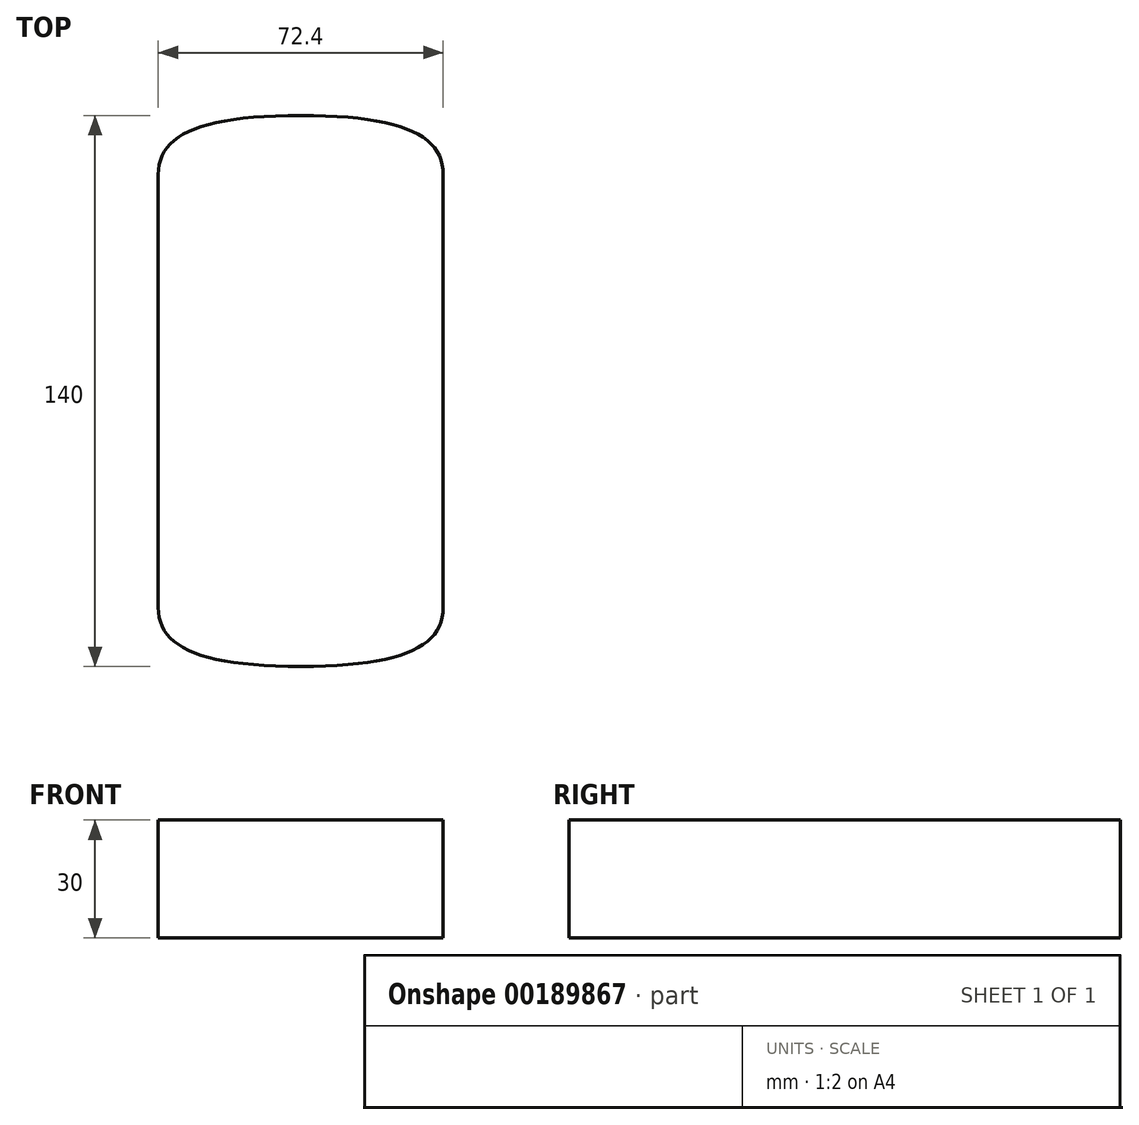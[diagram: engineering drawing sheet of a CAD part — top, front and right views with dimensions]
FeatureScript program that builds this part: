
annotation { "Feature Type Name" : "Feature", "Feature Type Description" : "" }
export const myFeature = defineFeature(function(context is Context, id is Id, definition is map)
    precondition{}
    {
        {
            var Q0;
            Q0=qCreatedBy(makeId("Top.planeOp"),FACE);
            var sketch = newSketch(context, id + "F0", { "sketchPlane" : qUnion([Q0])});
            skLineSegment(sketch, "E0", {"start": v(-36.2, 0) * mm, "end": v(-36.2, 55) * mm});
            skFitSpline(sketch, "E1", {"points": [v(-36.2, 55) * mm, v(0, 70) * mm], "startDerivative": vector(0, 30) * mm, "endDerivative": vector(76.78, 0) * mm});
            skLineSegment(sketch, "E2", {"start": v(0, 70) * mm, "end": v(0, 0) * mm});
            skLineSegment(sketch, "E3", {"start": v(0, 0) * mm, "end": v(-36.2, 0) * mm});
            skSolve(sketch);
        }
        {
            var Q0;
            Q0=makeQuery(id+"F0.imprint","IMPRINT",FACE,{"disambiguationData":[TD([[makeQuery(id+"F0.imprint","IMPRINT",EDGE,{"derivedFrom":sQuery(id+"F0.wireOp",EDGE,"E0")}),-1.0]])]});
            extrude(context, id + "F1", {"entities" : qUnion([Q0]), "depth" : 30 * mm});
        }
        {
            var Q0;
            Q0=makeQuery(id+"F1.opExtrude","SWEPT_BODY",BODY,{"disambiguationData":[OSD([sQuery(id+"F0.wireOp",EDGE,"E0"),sQuery(id+"F0.wireOp",EDGE,"E1"),sQuery(id+"F0.wireOp",EDGE,"E2"),sQuery(id+"F0.wireOp",EDGE,"E3")])]});
            var Q1;
            Q1=qCreatedBy(makeId("Right.planeOp"),FACE);
            mirror(context, id + "F2", {"operationType" : NewBodyOperationType.ADD, "entities" : qUnion([Q0]), "mirrorPlane" : qUnion([Q1])});
        }
        {
            var Q0;
            Q0=makeQuery(id+"F1.opExtrude","SWEPT_BODY",BODY,{"disambiguationData":[OSD([sQuery(id+"F0.wireOp",EDGE,"E0"),sQuery(id+"F0.wireOp",EDGE,"E1"),sQuery(id+"F0.wireOp",EDGE,"E2"),sQuery(id+"F0.wireOp",EDGE,"E3")])]});
            var Q1;
            Q1=qCreatedBy(makeId("Front.planeOp"),FACE);
            mirror(context, id + "F3", {"operationType" : NewBodyOperationType.ADD, "entities" : qUnion([Q0]), "mirrorPlane" : qUnion([Q1])});
        }
    });
